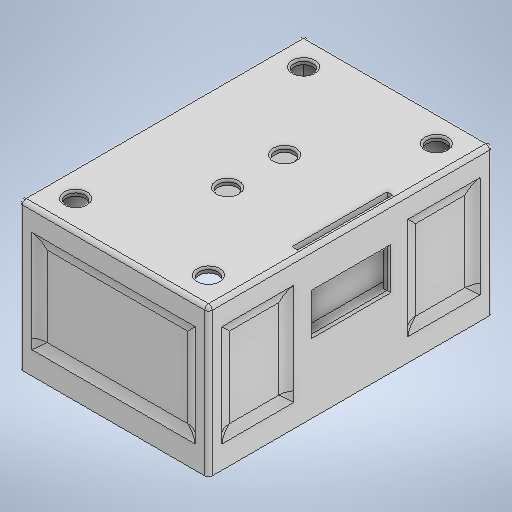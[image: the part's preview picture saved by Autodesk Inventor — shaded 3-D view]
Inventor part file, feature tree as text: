
AUTODESK INVENTOR PART (.ipt)
format: ipt  version: 2025 (Build 290162000, 162)  size: 933,376 bytes
history: native  units: mm
features: extrude x12, sketch x12, fillet x5, other x1
ambient origin geometry x8: Origin, YZ Plane, XZ Plane, XY Plane, X Axis, Y Axis, Z Axis, Center Point
bodies: Body1 (feature_tree)
feature tree (30):
  other  "ソリッド1"
  extrude  "側面"  Depth=150.0mm
  extrude  "上面"  Depth=100.0mm
  extrude  "接合部"  Depth=4.0mm
  extrude  "側面2"  Depth=4.0mm
  extrude  "はめ込み穴"  Depth=4.0mm
  extrude  "押し出し6"  Depth=1.0mm
  extrude  "押し出し7"  Depth=75.0mm TaperAngle=0.0deg
  extrude  "押し出し8"  Depth=2.5mm TaperAngle=0.0deg
  fillet  "フィレット1"  Radius=5.0mm
  fillet  "フィレット2"  Radius=40.0mm
  fillet  "フィレット3"  Radius=5.0mm
  extrude  "押し出し9"  Depth=56.0mm
  extrude  "押し出し10"  Depth=5.0mm
  extrude  "押し出し11"  Depth=5.0mm
  extrude  "押し出し12"  Depth=5.0mm
  fillet  "フィレット7"  Radius=75.0mm
  fillet  "フィレット8"  Radius=4.0mm
  sketch  "スケッチ1"
  sketch  "スケッチ2"
  sketch  "スケッチ3"
  sketch  "スケッチ4"
  sketch  "スケッチ5"
  sketch  "スケッチ7"
  sketch  "スケッチ8"
  sketch  "スケッチ9"
  sketch  "スケッチ10"
  sketch  "スケッチ11"
  sketch  "スケッチ12"
  sketch  "スケッチ13"
